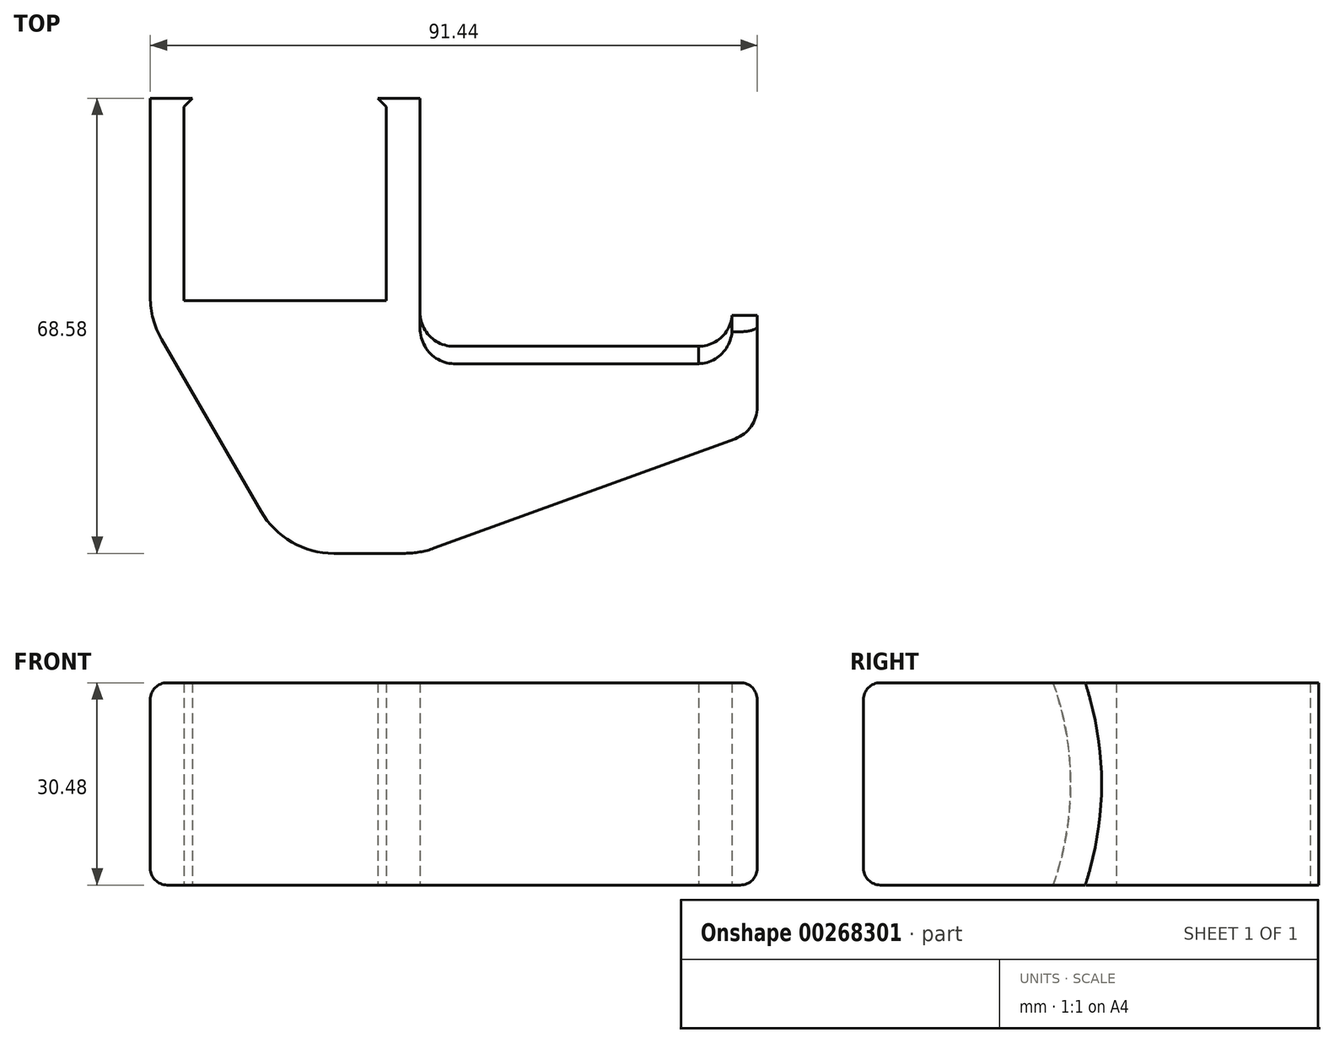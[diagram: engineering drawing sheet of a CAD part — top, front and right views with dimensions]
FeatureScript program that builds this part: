
annotation { "Feature Type Name" : "Feature", "Feature Type Description" : "" }
export const myFeature = defineFeature(function(context is Context, id is Id, definition is map)
    precondition{}
    {
        {
            var Q0;
            Q0=qCreatedBy(makeId("Top.planeOp"),FACE);
            var sketch = newSketch(context, id + "F0", { "sketchPlane" : qUnion([Q0])});
            skLineSegment(sketch, "E0.bottom", {"start": v(15.24, -15.24) * mm, "end": v(-15.24, -15.24) * mm});
            skLineSegment(sketch, "E0.left", {"start": v(15.24, -15.24) * mm, "end": v(15.24, 13.97) * mm});
            skLineSegment(sketch, "E0.right", {"start": v(-15.24, -15.24) * mm, "end": v(-15.24, 13.97) * mm});
            skPoint(sketch, "E0.middle", {"position": v(0, 0) * mm});
            skLineSegment(sketch, "E1", {"start": v(-15.24, 15.24) * mm, "end": v(-20.32, 15.24) * mm});
            skLineSegment(sketch, "E2", {"start": v(-20.32, 15.24) * mm, "end": v(-20.32, -14.74) * mm});
            skLineSegment(sketch, "E3", {"start": v(-18.62, -21.1) * mm, "end": v(-3.67, -47) * mm});
            skLineSegment(sketch, "E4", {"start": v(7.33, -53.34) * mm, "end": v(18.08, -53.34) * mm});
            skLineSegment(sketch, "E5", {"start": v(22.42, -52.57) * mm, "end": v(67.78, -36.07) * mm});
            skLineSegment(sketch, "E6", {"start": v(71.12, -31.3) * mm, "end": v(71.12, -22.15) * mm});
            skLineSegment(sketch, "E7", {"start": v(71.12, -22.15) * mm, "end": v(20.32, -22.15) * mm});
            skLineSegment(sketch, "E8", {"start": v(20.32, -22.15) * mm, "end": v(20.32, 15.24) * mm});
            skLineSegment(sketch, "E9", {"start": v(20.32, 15.24) * mm, "end": v(15.24, 15.24) * mm});
            skPoint(sketch, "E10.visualSharp", {"position": v(-20.32, -18.14) * mm});
            skArc(sketch, "E10.filletArc", {"start": v(-20.32, -14.74) * mm, "mid": v(-19.89, -18.03) * mm, "end": v(-18.62, -21.1) * mm});
            skPoint(sketch, "E11.visualSharp", {"position": v(0, -53.34) * mm});
            skArc(sketch, "E11.filletArc", {"start": v(-3.67, -47) * mm, "mid": v(0.98, -51.64) * mm, "end": v(7.33, -53.34) * mm});
            skPoint(sketch, "E12.visualSharp", {"position": v(20.32, -53.34) * mm});
            skArc(sketch, "E12.filletArc", {"start": v(18.08, -53.34) * mm, "mid": v(20.29, -53.15) * mm, "end": v(22.42, -52.57) * mm});
            skPoint(sketch, "E13.visualSharp", {"position": v(71.12, -34.85) * mm});
            skArc(sketch, "E13.filletArc", {"start": v(67.78, -36.07) * mm, "mid": v(70.2, -34.2) * mm, "end": v(71.12, -31.3) * mm});
            skLineSegment(sketch, "E14", {"start": v(-15.24, 15.24) * mm, "end": v(-13.97, 15.24) * mm});
            skLineSegment(sketch, "E15", {"start": v(-13.97, 15.24) * mm, "end": v(-15.24, 13.97) * mm});
            skLineSegment(sketch, "E16", {"start": v(15.24, 15.24) * mm, "end": v(13.97, 15.24) * mm});
            skLineSegment(sketch, "E17", {"start": v(13.97, 15.24) * mm, "end": v(15.24, 13.97) * mm});
            skSolve(sketch);
        }
        {
            var Q0;
            Q0 = qSketchRegion(id + "F0", true);
            extrude(context, id + "F1", {"entities" : qUnion([Q0]), "depth" : 30.48 * mm});
        }
        {
            var Q0;
            Q0=makeQuery(id+"F1.opExtrude","SWEPT_FACE",FACE,{"disambiguationData":[OSD([sQuery(id+"F0.wireOp",EDGE,"E6")])]});
            var sketch = newSketch(context, id + "F2", { "sketchPlane" : qUnion([Q0])});
            skArc(sketch, "E18", {"start": v(-24.77, 30.48) * mm, "mid": v(-22.15, 15.24) * mm, "end": v(-24.77, 0) * mm});
            skLineSegment(sketch, "E19", {"start": v(-24.77, 30.48) * mm, "end": v(-15.72, 30.48) * mm});
            skLineSegment(sketch, "E20", {"start": v(-15.72, 30.48) * mm, "end": v(-15.72, 0) * mm});
            skLineSegment(sketch, "E21", {"start": v(-15.72, 0) * mm, "end": v(-24.77, 0) * mm});
            skSolve(sketch);
        }
        {
            var Q0;
            Q0 = qSketchRegion(id + "F2", true);
            extrude(context, id + "F3", {"entities" : qUnion([Q0]), "operationType" : NewBodyOperationType.REMOVE, "oppositeDirection" : true, "depth" : 50.8 * mm});
        }
        {
            var Q0;
            Q0=qCreatedBy(makeId("Front.planeOp"),FACE);
            cPlane(context, id + "F4", {"entities" : qUnion([Q0]), "cplaneType" : CPlaneType.OFFSET, "offset" : 25.4 * mm, "width" : 152.4 * mm, "height" : 152.4 * mm});
        }
        {
            var Q0;
            Q0=qCreatedBy(id+"F4.planeOp",FACE);
            var sketch = newSketch(context, id + "F5", { "sketchPlane" : qUnion([Q0])});
            skLineSegment(sketch, "E22.bottom", {"start": v(71.12, 30.48) * mm, "end": v(67.31, 30.48) * mm});
            skLineSegment(sketch, "E22.top", {"start": v(71.12, 0) * mm, "end": v(67.31, 0) * mm});
            skLineSegment(sketch, "E22.left", {"start": v(71.12, 30.48) * mm, "end": v(71.12, 0) * mm});
            skLineSegment(sketch, "E22.right", {"start": v(67.31, 30.48) * mm, "end": v(67.31, 0) * mm});
            skSolve(sketch);
        }
        {
            var Q0;
            Q0 = qSketchRegion(id + "F5", true);
            extrude(context, id + "F6", {"entities" : qUnion([Q0]), "operationType" : NewBodyOperationType.ADD, "oppositeDirection" : true, "depth" : 10.16 * mm});
        }
        {
            var Q0;
            Q0=makeQuery(id+"F6.boolean.opBoolean","MERGE",FACE,{"derivedFrom":[makeQuery(id+"F1.opExtrude","SWEPT_FACE",FACE,{"disambiguationData":[OSD([sQuery(id+"F0.wireOp",EDGE,"E6")])]}),makeQuery(id+"F6.opExtrude","SWEPT_FACE",FACE,{"disambiguationData":[OSD([sQuery(id+"F5.wireOp",EDGE,"E22.left")])]})]});
            var sketch = newSketch(context, id + "F7", { "sketchPlane" : qUnion([Q0])});
            skArc(sketch, "E23", {"start": v(-19.95, 30.48) * mm, "mid": v(-17.48, 15.24) * mm, "end": v(-19.95, 0) * mm});
            skLineSegment(sketch, "E24", {"start": v(-19.95, 30.48) * mm, "end": v(-9.54, 30.48) * mm});
            skLineSegment(sketch, "E25", {"start": v(-9.54, 30.48) * mm, "end": v(-9.54, 0) * mm});
            skLineSegment(sketch, "E26", {"start": v(-9.54, 0) * mm, "end": v(-19.95, 0) * mm});
            skSolve(sketch);
        }
        {
            var Q0;
            Q0 = qSketchRegion(id + "F7", true);
            extrude(context, id + "F8", {"entities" : qUnion([Q0]), "operationType" : NewBodyOperationType.REMOVE, "oppositeDirection" : true, "depth" : 25.4 * mm});
        }
        {
            var Q0;
            Q0=makeQuery(id+"F3.boolean.opBoolean","COPY",EDGE,{"derivedFrom":makeQuery(id+"F3.opExtrude","CAP_EDGE",EDGE,{"disambiguationData":[OSD([sQuery(id+"F2.wireOp",EDGE,"E18")])],"isStart":false})});
            var Q1;
            Q1=makeQuery(id+"F6.boolean.opBoolean","INTERSECT",EDGE,{"derivedFrom":[makeQuery(id+"F3.boolean.opBoolean","COPY",FACE,{"derivedFrom":makeQuery(id+"F3.opExtrude","SWEPT_FACE",FACE,{"disambiguationData":[OSD([sQuery(id+"F2.wireOp",EDGE,"E18")])]})}),makeQuery(id+"F6.opExtrude","SWEPT_FACE",FACE,{"disambiguationData":[OSD([sQuery(id+"F5.wireOp",EDGE,"E22.right")])]})]});
            fillet(context, id + "F9", {"entities" : qUnion([Q0, Q1]), "radius" : 5.08 * mm, "tangentPropagation" : true, "allowEdgeOverflow" : false});
        }
        {
            var Q0;
            Q0=makeQuery(id+"F1.opExtrude","CAP_EDGE",EDGE,{"disambiguationData":[OSD([sQuery(id+"F0.wireOp",EDGE,"E3")])],"isStart":false});
            var Q1;
            Q1=makeQuery(id+"F1.opExtrude","CAP_EDGE",EDGE,{"disambiguationData":[OSD([sQuery(id+"F0.wireOp",EDGE,"E5")])],"isStart":true});
            var Q2;
            Q2=makeQuery(id+"F3.boolean.opBoolean","MERGE",EDGE,{"derivedFrom":[makeQuery(id+"F1.opExtrude","CAP_EDGE",EDGE,{"disambiguationData":[OSD([sQuery(id+"F0.wireOp",EDGE,"E8")])],"isStart":false}),makeQuery(id+"F3.opExtrude","CAP_EDGE",EDGE,{"disambiguationData":[OSD([sQuery(id+"F2.wireOp",EDGE,"E19")])],"isStart":false})]});
            var Q3;
            Q3=makeQuery(id+"F3.boolean.opBoolean","MERGE",EDGE,{"derivedFrom":[makeQuery(id+"F1.opExtrude","CAP_EDGE",EDGE,{"disambiguationData":[OSD([sQuery(id+"F0.wireOp",EDGE,"E8")])],"isStart":true}),makeQuery(id+"F3.opExtrude","CAP_EDGE",EDGE,{"disambiguationData":[OSD([sQuery(id+"F2.wireOp",EDGE,"E21")])],"isStart":false})]});
            fillet(context, id + "F10", {"entities" : qUnion([Q0, Q1, Q2, Q3]), "radius" : 2.54 * mm, "tangentPropagation" : true, "allowEdgeOverflow" : false});
        }
    });
